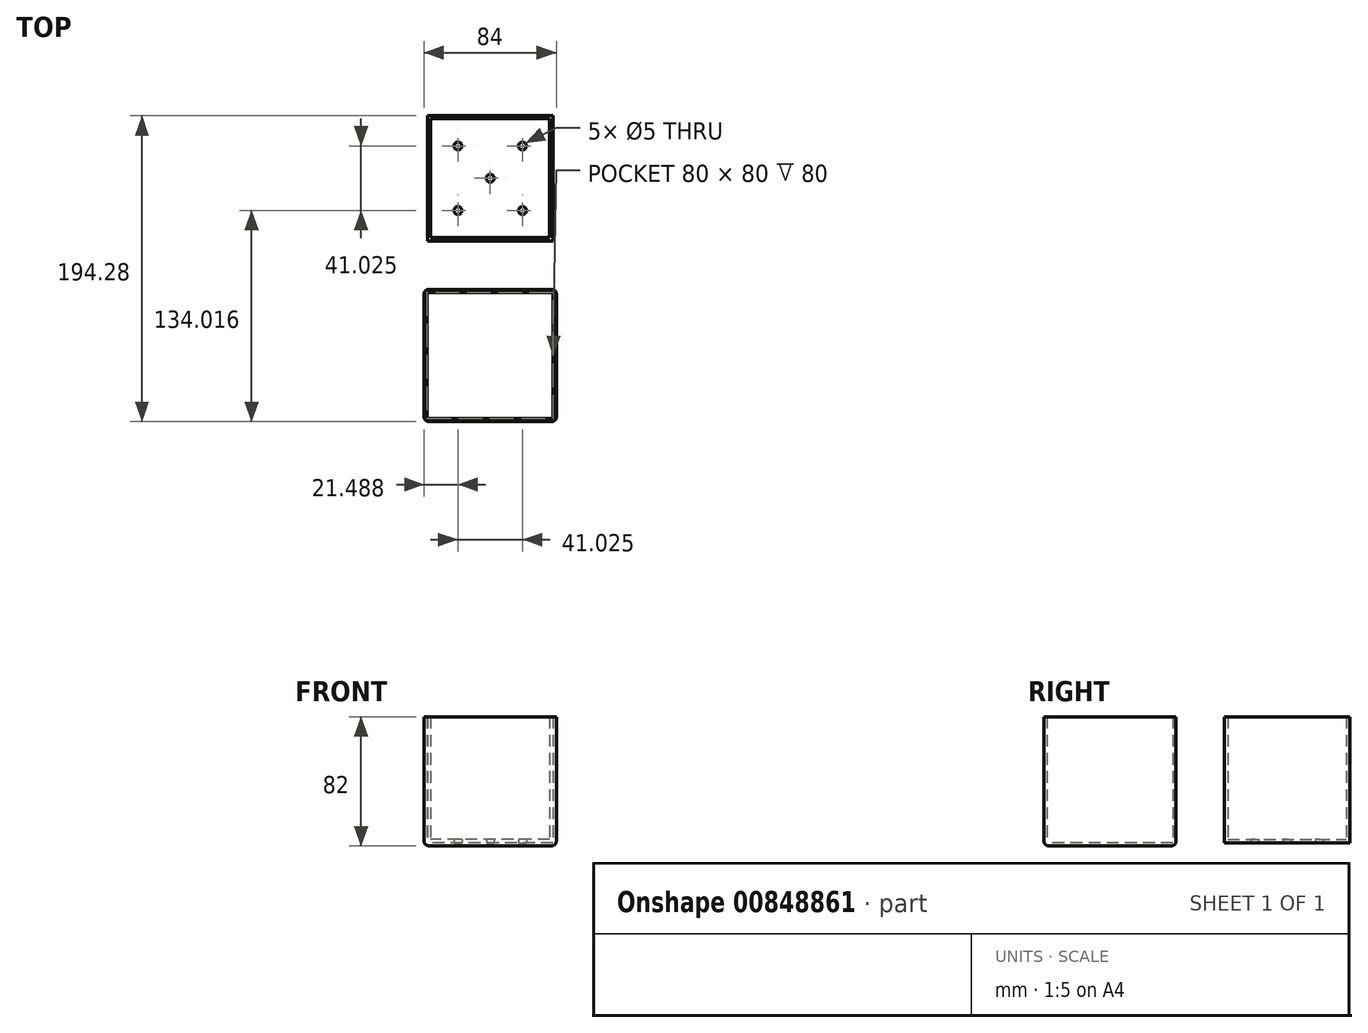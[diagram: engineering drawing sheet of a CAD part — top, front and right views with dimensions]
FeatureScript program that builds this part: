
annotation { "Feature Type Name" : "Feature", "Feature Type Description" : "" }
export const myFeature = defineFeature(function(context is Context, id is Id, definition is map)
    precondition{}
    {
        {
            var Q0;
            Q0=qCreatedBy(makeId("Top.planeOp"),FACE);
            var sketch = newSketch(context, id + "F0", { "sketchPlane" : qUnion([Q0])});
            skLineSegment(sketch, "E0.bottom", {"start": v(40, 40) * mm, "end": v(-40, 40) * mm});
            skLineSegment(sketch, "E0.top", {"start": v(40, -40) * mm, "end": v(-40, -40) * mm});
            skLineSegment(sketch, "E0.left", {"start": v(40, 40) * mm, "end": v(40, -40) * mm});
            skLineSegment(sketch, "E0.right", {"start": v(-40, 40) * mm, "end": v(-40, -40) * mm});
            skPoint(sketch, "E0.middle", {"position": v(0, 0) * mm});
            skSolve(sketch);
        }
        {
            var Q0;
            Q0=makeQuery(id+"F0.imprint","IMPRINT",FACE,{"disambiguationData":[TD([[makeQuery(id+"F0.imprint","IMPRINT",EDGE,{"derivedFrom":sQuery(id+"F0.wireOp",EDGE,"E0.bottom")}),1.0]])]});
            extrude(context, id + "F1", {"entities" : qUnion([Q0]), "depth" : 80 * mm, "offsetDistance" : 25 * mm});
        }
        {
            var Q0;
            Q0=makeQuery(id+"F1.opExtrude","CAP_FACE",FACE,{"disambiguationData":[OSD([sQuery(id+"F0.wireOp",EDGE,"E0.bottom"),sQuery(id+"F0.wireOp",EDGE,"E0.top"),sQuery(id+"F0.wireOp",EDGE,"E0.left"),sQuery(id+"F0.wireOp",EDGE,"E0.right")])],"isStart":false});
            shell(context, id + "F2", {"entities" : qUnion([Q0]), "thickness" : 2 * mm, "oppositeDirection" : true});
        }
        {
            var Q0;
            Q0=qCreatedBy(makeId("Top.planeOp"),FACE);
            var sketch = newSketch(context, id + "F3", { "sketchPlane" : qUnion([Q0])});
            skLineSegment(sketch, "E1.bottom", {"start": v(39.75, 72.78) * mm, "end": v(-39.75, 72.78) * mm});
            skLineSegment(sketch, "E1.top", {"start": v(39.75, 152.28) * mm, "end": v(-39.75, 152.28) * mm});
            skLineSegment(sketch, "E1.left", {"start": v(39.75, 72.78) * mm, "end": v(39.75, 152.28) * mm});
            skLineSegment(sketch, "E1.right", {"start": v(-39.75, 72.78) * mm, "end": v(-39.75, 152.28) * mm});
            skPoint(sketch, "E1.middle", {"position": v(0, 112.53) * mm});
            skSolve(sketch);
        }
        {
            var Q0;
            Q0=makeQuery(id+"F3.imprint","IMPRINT",FACE,{"disambiguationData":[TD([[makeQuery(id+"F3.imprint","IMPRINT",EDGE,{"derivedFrom":sQuery(id+"F3.wireOp",EDGE,"E1.bottom")}),-1.0]])]});
            extrude(context, id + "F4", {"entities" : qUnion([Q0]), "depth" : 80 * mm, "offsetDistance" : 25 * mm});
        }
        {
            var Q0;
            Q0=makeQuery(id+"F4.opExtrude","CAP_FACE",FACE,{"disambiguationData":[OSD([sQuery(id+"F3.wireOp",EDGE,"E1.bottom"),sQuery(id+"F3.wireOp",EDGE,"E1.top"),sQuery(id+"F3.wireOp",EDGE,"E1.left"),sQuery(id+"F3.wireOp",EDGE,"E1.right")])],"isStart":false});
            shell(context, id + "F5", {"entities" : qUnion([Q0]), "thickness" : 2 * mm});
        }
        {
            var Q0;
            Q0=makeQuery(id+"F1.opExtrude","SWEPT_EDGE",EDGE,{"disambiguationData":[OSD([sQuery(id+"F0.wireOp",EDGE,"E0.top"),sQuery(id+"F0.wireOp",EDGE,"E0.left")])]});
            var Q1;
            Q1=makeQuery(id+"F1.opExtrude","SWEPT_EDGE",EDGE,{"disambiguationData":[OSD([sQuery(id+"F0.wireOp",EDGE,"E0.bottom"),sQuery(id+"F0.wireOp",EDGE,"E0.left")])]});
            var Q2;
            Q2=makeQuery(id+"F1.opExtrude","SWEPT_EDGE",EDGE,{"disambiguationData":[OSD([sQuery(id+"F0.wireOp",EDGE,"E0.bottom"),sQuery(id+"F0.wireOp",EDGE,"E0.right")])]});
            var Q3;
            Q3=makeQuery(id+"F1.opExtrude","SWEPT_EDGE",EDGE,{"disambiguationData":[OSD([sQuery(id+"F0.wireOp",EDGE,"E0.top"),sQuery(id+"F0.wireOp",EDGE,"E0.right")])]});
            fillet(context, id + "F6", {"entities" : qUnion([Q0, Q1, Q2, Q3]), "radius" : 3 * mm, "tangentPropagation" : true, "allowEdgeOverflow" : false});
        }
        {
            var Q0;
            Q0=makeQuery(id+"F1.opExtrude","CAP_EDGE",EDGE,{"disambiguationData":[OSD([sQuery(id+"F0.wireOp",EDGE,"E0.bottom")])],"isStart":true});
            fillet(context, id + "F7", {"entities" : qUnion([Q0]), "radius" : 3 * mm, "tangentPropagation" : true, "allowEdgeOverflow" : false});
        }
        {
            var Q0;
            Q0=makeQuery(id+"F4.opExtrude","CAP_FACE",FACE,{"disambiguationData":[OSD([sQuery(id+"F3.wireOp",EDGE,"E1.bottom"),sQuery(id+"F3.wireOp",EDGE,"E1.top"),sQuery(id+"F3.wireOp",EDGE,"E1.left"),sQuery(id+"F3.wireOp",EDGE,"E1.right")])],"isStart":true});
            var sketch = newSketch(context, id + "F8", { "sketchPlane" : qUnion([Q0])});
            skLineSegment(sketch, "E2.bottom", {"start": v(-39.75, -152.28) * mm, "end": v(39.75, -152.28) * mm});
            skLineSegment(sketch, "E2.top", {"start": v(-39.75, -72.78) * mm, "end": v(39.75, -72.78) * mm});
            skLineSegment(sketch, "E2.left", {"start": v(-39.75, -152.28) * mm, "end": v(-39.75, -72.78) * mm});
            skLineSegment(sketch, "E2.right", {"start": v(39.75, -152.28) * mm, "end": v(39.75, -72.78) * mm});
            skPoint(sketch, "E2.middle", {"position": v(0, -112.53) * mm});
            skPoint(sketch, "E3.third.point", {"position": v(0, -72.78) * mm});
            skPoint(sketch, "E4.third.point", {"position": v(-39.75, -112.53) * mm});
            skPoint(sketch, "E5.third.point", {"position": v(0, -152.28) * mm});
            skCircle(sketch, "E6", {"center": v(20.51, -133.04) * mm, "radius": 2.5 * mm});
            skCircle(sketch, "E7", {"center": v(-20.51, -133.04) * mm, "radius": 2.5 * mm});
            skCircle(sketch, "E8", {"center": v(-20.51, -92.02) * mm, "radius": 2.5 * mm});
            skCircle(sketch, "E9", {"center": v(20.51, -92.02) * mm, "radius": 2.5 * mm});
            skCircle(sketch, "E10", {"center": v(0, -112.53) * mm, "radius": 2.5 * mm});
            skSolve(sketch);
        }
        {
            var Q0;
            Q0=makeQuery(id+"F8.imprint","IMPRINT",FACE,{"disambiguationData":[TD([[makeQuery(id+"F8.imprint","IMPRINT",EDGE,{"derivedFrom":sQuery(id+"F8.wireOp",EDGE,"E6")}),1.0]])]});
            var Q1;
            Q1=makeQuery(id+"F8.imprint","IMPRINT",FACE,{"disambiguationData":[TD([[makeQuery(id+"F8.imprint","IMPRINT",EDGE,{"derivedFrom":sQuery(id+"F8.wireOp",EDGE,"E7")}),1.0]])]});
            var Q2;
            Q2=makeQuery(id+"F8.imprint","IMPRINT",FACE,{"disambiguationData":[TD([[makeQuery(id+"F8.imprint","IMPRINT",EDGE,{"derivedFrom":sQuery(id+"F8.wireOp",EDGE,"E8")}),1.0]])]});
            var Q3;
            Q3=makeQuery(id+"F8.imprint","IMPRINT",FACE,{"disambiguationData":[TD([[makeQuery(id+"F8.imprint","IMPRINT",EDGE,{"derivedFrom":sQuery(id+"F8.wireOp",EDGE,"E10")}),1.0]])]});
            var Q4;
            Q4=makeQuery(id+"F8.imprint","IMPRINT",FACE,{"disambiguationData":[TD([[makeQuery(id+"F8.imprint","IMPRINT",EDGE,{"derivedFrom":sQuery(id+"F8.wireOp",EDGE,"E9")}),1.0]])]});
            extrude(context, id + "F9", {"entities" : qUnion([Q0, Q1, Q2, Q3, Q4]), "operationType" : NewBodyOperationType.REMOVE, "oppositeDirection" : true, "depth" : 2.05 * mm, "offsetDistance" : 25 * mm});
        }
    });
